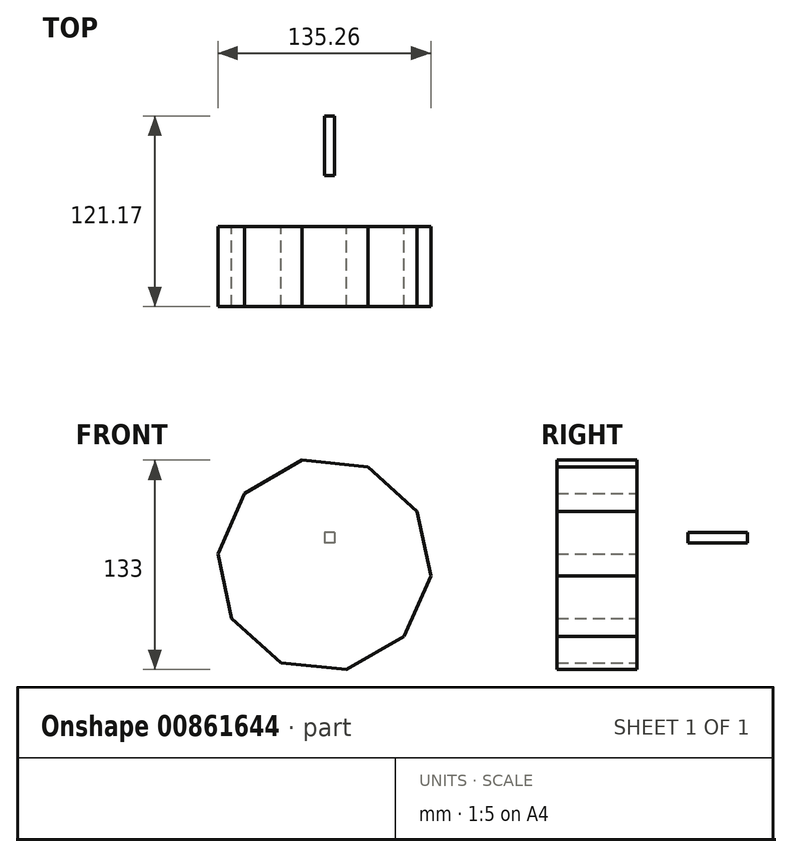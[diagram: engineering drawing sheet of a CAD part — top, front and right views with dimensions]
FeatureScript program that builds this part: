
annotation { "Feature Type Name" : "Feature", "Feature Type Description" : "" }
export const myFeature = defineFeature(function(context is Context, id is Id, definition is map)
    precondition{}
    {
        {
            var Q0;
            Q0=qCreatedBy(makeId("Front.planeOp"),FACE);
            var sketch = newSketch(context, id + "F0", { "sketchPlane" : qUnion([Q0])});
            skCircle(sketch, "E0.cCircle", {"center": v(0, 0) * mm, "radius": 64.67 * mm, "construction": true});
            skLineSegment(sketch, "E0.0", {"start": v(-50.57, 45.46) * mm, "end": v(-14.19, 66.5) * mm});
            skLineSegment(sketch, "E0.1", {"start": v(-14.19, 66.5) * mm, "end": v(27.6, 62.14) * mm});
            skLineSegment(sketch, "E0.2", {"start": v(27.6, 62.14) * mm, "end": v(58.86, 34.04) * mm});
            skLineSegment(sketch, "E0.3", {"start": v(58.86, 34.04) * mm, "end": v(67.63, -7.05) * mm});
            skLineSegment(sketch, "E0.4", {"start": v(67.63, -7.05) * mm, "end": v(50.57, -45.46) * mm});
            skLineSegment(sketch, "E0.5", {"start": v(50.57, -45.46) * mm, "end": v(14.19, -66.5) * mm});
            skLineSegment(sketch, "E0.6", {"start": v(14.19, -66.5) * mm, "end": v(-27.6, -62.14) * mm});
            skLineSegment(sketch, "E0.7", {"start": v(-27.6, -62.14) * mm, "end": v(-58.86, -34.04) * mm});
            skLineSegment(sketch, "E0.8", {"start": v(-58.86, -34.04) * mm, "end": v(-67.63, 7.05) * mm});
            skLineSegment(sketch, "E0.9", {"start": v(-67.63, 7.05) * mm, "end": v(-50.57, 45.46) * mm});
            skPoint(sketch, "E0.0.midPoint", {"position": v(-32.38, 55.98) * mm});
            skSolve(sketch);
        }
        {
            var Q0;
            Q0 = qSketchRegion(id + "F0", true);
            extrude(context, id + "F1", {"entities" : qUnion([Q0]), "depth" : 50.8 * mm, "offsetDistance" : 25.4 * mm});
        }
        {
            var Q0;
            Q0=qCreatedBy(makeId("Right.planeOp"),FACE);
            var sketch = newSketch(context, id + "F2", { "sketchPlane" : qUnion([Q0])});
            skLineSegment(sketch, "E1.bottom", {"start": v(32.38, 20.55) * mm, "end": v(70.37, 20.55) * mm});
            skLineSegment(sketch, "E1.top", {"start": v(32.38, 14.04) * mm, "end": v(70.37, 14.04) * mm});
            skLineSegment(sketch, "E1.left", {"start": v(32.38, 20.55) * mm, "end": v(32.38, 14.04) * mm});
            skLineSegment(sketch, "E1.right", {"start": v(70.37, 20.55) * mm, "end": v(70.37, 14.04) * mm});
            skSolve(sketch);
        }
        {
            var Q0;
            Q0 = qSketchRegion(id + "F2", true);
            extrude(context, id + "F3", {"entities" : qUnion([Q0]), "depth" : 6.35 * mm, "offsetDistance" : 25.4 * mm});
        }
    });
